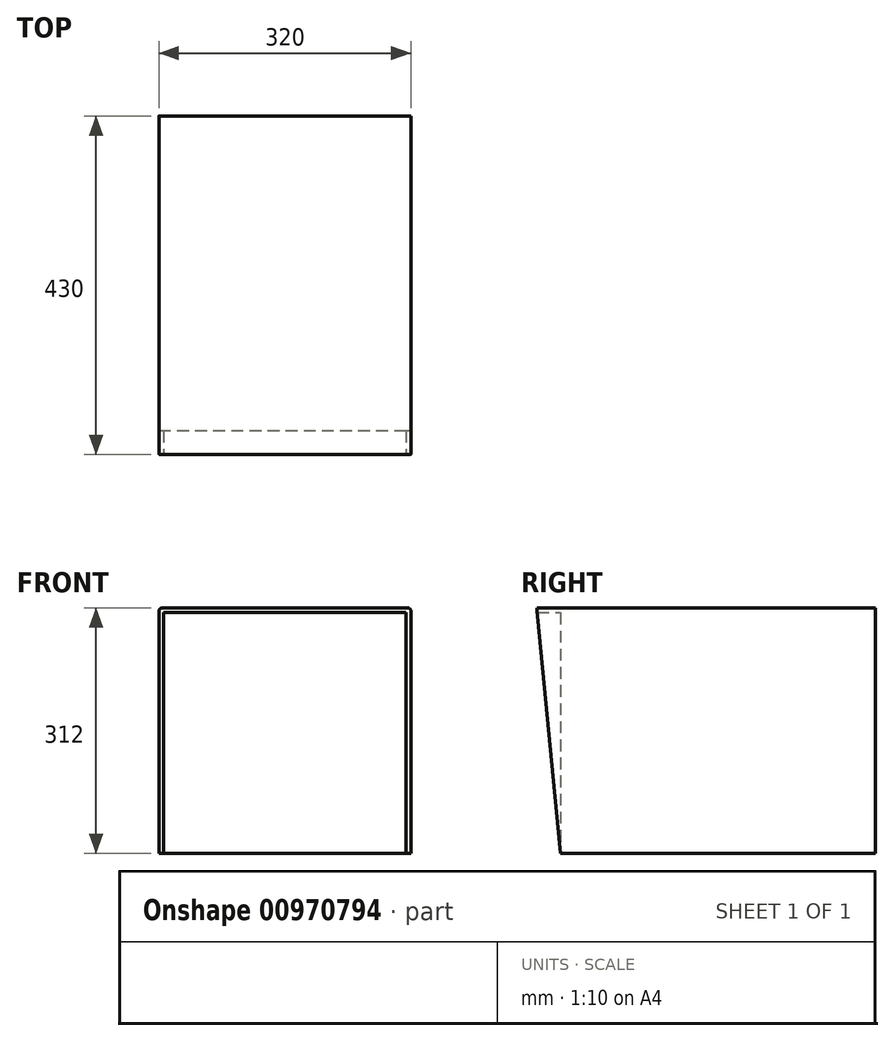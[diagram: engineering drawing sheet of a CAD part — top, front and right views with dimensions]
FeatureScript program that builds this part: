
annotation { "Feature Type Name" : "Feature", "Feature Type Description" : "" }
export const myFeature = defineFeature(function(context is Context, id is Id, definition is map)
    precondition{}
    {
        {
            var Q0;
            Q0=qCreatedBy(makeId("Right.planeOp"),FACE);
            var sketch = newSketch(context, id + "F0", { "sketchPlane" : qUnion([Q0])});
            skLineSegment(sketch, "E0.bottom", {"start": v(0, 0) * mm, "end": v(-430, 0) * mm});
            skLineSegment(sketch, "E0.top", {"start": v(0, -312) * mm, "end": v(-400, -312) * mm});
            skLineSegment(sketch, "E0.left", {"start": v(0, 0) * mm, "end": v(0, -312) * mm});
            skLineSegment(sketch, "E1", {"start": v(-400, -312) * mm, "end": v(-430, 0) * mm});
            skSolve(sketch);
        }
        {
            var Q0;
            Q0=makeQuery(id+"F0.imprint","IMPRINT",FACE,{"disambiguationData":[TD([[makeQuery(id+"F0.imprint","IMPRINT",EDGE,{"derivedFrom":sQuery(id+"F0.wireOp",EDGE,"E0.bottom")}),1.0]])]});
            extrude(context, id + "F1", {"entities" : qUnion([Q0]), "depth" : 320 * mm, "offsetDistance" : 25 * mm});
        }
        {
            var Q0;
            Q0=makeQuery(id+"F1.opExtrude","SWEPT_FACE",FACE,{"disambiguationData":[OSD([sQuery(id+"F0.wireOp",EDGE,"E0.top")])]});
            var sketch = newSketch(context, id + "F2", { "sketchPlane" : qUnion([Q0])});
            skLineSegment(sketch, "E2.bottom", {"start": v(6, 400) * mm, "end": v(314, 400) * mm});
            skLineSegment(sketch, "E2.top", {"start": v(6, 430) * mm, "end": v(314, 430) * mm});
            skLineSegment(sketch, "E2.left", {"start": v(6, 400) * mm, "end": v(6, 430) * mm});
            skLineSegment(sketch, "E2.right", {"start": v(314, 400) * mm, "end": v(314, 430) * mm});
            skSolve(sketch);
        }
        {
            var Q0;
            Q0=makeQuery(id+"F2.imprint","IMPRINT",FACE,{"disambiguationData":[TD([[makeQuery(id+"F2.imprint","IMPRINT",EDGE,{"derivedFrom":sQuery(id+"F2.wireOp",EDGE,"E2.bottom")}),-1.0]])]});
            var Q1;
            Q1=makeQuery(id+"F1.opExtrude","SWEPT_FACE",FACE,{"disambiguationData":[OSD([sQuery(id+"F0.wireOp",EDGE,"E0.bottom")])]});
            extrude(context, id + "F3", {"entities" : qUnion([Q0]), "operationType" : NewBodyOperationType.REMOVE, "endBound" : BoundingType.UP_TO_SURFACE, "oppositeDirection" : true, "depth" : 25 * mm, "endBoundEntityFace" : qUnion([Q1]), "hasOffset" : true, "offsetDistance" : 6 * mm});
        }
        {
            var Q0;
            Q0=makeQuery(id+"F1.opExtrude","CAP_EDGE",EDGE,{"disambiguationData":[OSD([sQuery(id+"F0.wireOp",EDGE,"E0.bottom")])],"isStart":true});
            var Q1;
            Q1=makeQuery(id+"F1.opExtrude","CAP_EDGE",EDGE,{"disambiguationData":[OSD([sQuery(id+"F0.wireOp",EDGE,"E0.bottom")])],"isStart":false});
            fillet(context, id + "F4", {"entities" : qUnion([Q0, Q1]), "radius" : 4 * mm, "tangentPropagation" : true, "allowEdgeOverflow" : false});
        }
    });
